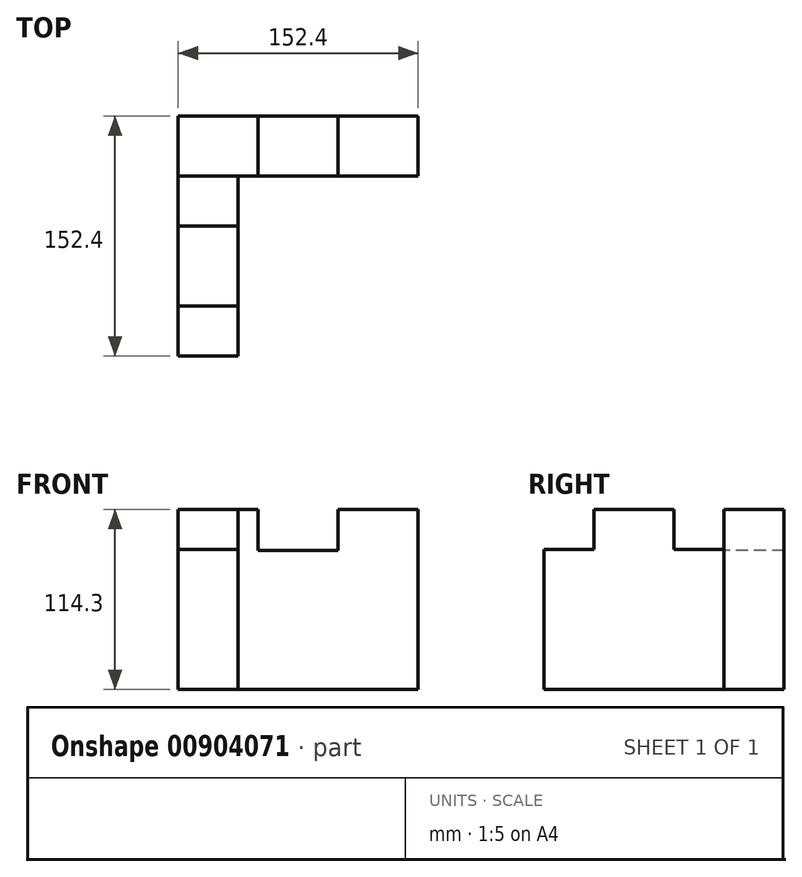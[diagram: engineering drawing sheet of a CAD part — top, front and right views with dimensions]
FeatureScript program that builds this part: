
annotation { "Feature Type Name" : "Feature", "Feature Type Description" : "" }
export const myFeature = defineFeature(function(context is Context, id is Id, definition is map)
    precondition{}
    {
        {
            var Q0;
            Q0=qCreatedBy(makeId("Front.planeOp"),FACE);
            var sketch = newSketch(context, id + "F0", { "sketchPlane" : qUnion([Q0])});
            skLineSegment(sketch, "E0.bottom", {"start": v(-76.2, 57.15) * mm, "end": v(76.2, 57.15) * mm});
            skLineSegment(sketch, "E0.top", {"start": v(-76.2, -57.15) * mm, "end": v(76.2, -57.15) * mm});
            skLineSegment(sketch, "E0.left", {"start": v(-76.2, 57.15) * mm, "end": v(-76.2, -57.15) * mm});
            skLineSegment(sketch, "E0.right", {"start": v(76.2, 57.15) * mm, "end": v(76.2, -57.15) * mm});
            skPoint(sketch, "E0.middle", {"position": v(0, 0) * mm});
            skSolve(sketch);
        }
        {
            var Q0;
            Q0=makeQuery(id+"F0.imprint","IMPRINT",FACE,{"disambiguationData":[TD([[makeQuery(id+"F0.imprint","IMPRINT",EDGE,{"derivedFrom":sQuery(id+"F0.wireOp",EDGE,"E0.bottom")}),-1.0]])]});
            extrude(context, id + "F1", {"entities" : qUnion([Q0]), "depth" : 152.4 * mm, "offsetDistance" : 25.4 * mm});
        }
        {
            var Q0;
            Q0=makeQuery(id+"F1.opExtrude","CAP_FACE",FACE,{"disambiguationData":[OSD([sQuery(id+"F0.wireOp",EDGE,"E0.bottom"),sQuery(id+"F0.wireOp",EDGE,"E0.top"),sQuery(id+"F0.wireOp",EDGE,"E0.left"),sQuery(id+"F0.wireOp",EDGE,"E0.right")])],"isStart":false});
            var sketch = newSketch(context, id + "F2", { "sketchPlane" : qUnion([Q0])});
            skLineSegment(sketch, "E1", {"start": v(-76.2, 57.15) * mm, "end": v(-38.1, 57.15) * mm});
            skLineSegment(sketch, "E2", {"start": v(-38.1, 57.15) * mm, "end": v(-38.1, -57.15) * mm});
            skSolve(sketch);
        }
        {
            var Q0;
            Q0 = qSketchRegion(id + "F2", true);
            var Q1;
            {var subQ0=sQuery(id+"F2.wireOp",EDGE,"E2");Q1=makeQuery(id+"F2.imprint","IMPRINT",FACE,{"disambiguationData":[TD([[makeQuery(id+"F2.imprint","IMPRINT",EDGE,{"derivedFrom":subQ0}),1.0]])]});}
            extrude(context, id + "F3", {"entities" : qUnion([Q0, Q1]), "operationType" : NewBodyOperationType.REMOVE, "oppositeDirection" : true, "depth" : 114.3 * mm, "offsetDistance" : 25.4 * mm});
        }
        {
            var Q0;
            Q0=makeQuery(id+"F1.opExtrude","CAP_FACE",FACE,{"disambiguationData":[OSD([sQuery(id+"F0.wireOp",EDGE,"E0.bottom"),sQuery(id+"F0.wireOp",EDGE,"E0.top"),sQuery(id+"F0.wireOp",EDGE,"E0.left"),sQuery(id+"F0.wireOp",EDGE,"E0.right")])],"isStart":false});
            var sketch = newSketch(context, id + "F4", { "sketchPlane" : qUnion([Q0])});
            skLineSegment(sketch, "E3.bottom", {"start": v(-76.2, 57.15) * mm, "end": v(-38.1, 57.15) * mm});
            skLineSegment(sketch, "E3.top", {"start": v(-76.2, 31.75) * mm, "end": v(-38.1, 31.75) * mm});
            skLineSegment(sketch, "E3.left", {"start": v(-76.2, 57.15) * mm, "end": v(-76.2, 31.75) * mm});
            skLineSegment(sketch, "E3.right", {"start": v(-38.1, 57.15) * mm, "end": v(-38.1, 31.75) * mm});
            skSolve(sketch);
        }
        {
            var Q0;
            Q0=makeQuery(id+"F4.imprint","IMPRINT",FACE,{"disambiguationData":[TD([[makeQuery(id+"F4.imprint","IMPRINT",EDGE,{"derivedFrom":sQuery(id+"F4.wireOp",EDGE,"E3.bottom")}),-1.0]])]});
            extrude(context, id + "F5", {"entities" : qUnion([Q0]), "operationType" : NewBodyOperationType.REMOVE, "oppositeDirection" : true, "depth" : 31.75 * mm, "offsetDistance" : 25.4 * mm});
        }
        {
            var Q0;
            Q0=makeQuery(id+"F3.boolean.opBoolean","COPY",FACE,{"derivedFrom":makeQuery(id+"F3.opExtrude","SWEPT_FACE",FACE,{"disambiguationData":[OSD([sQuery(id+"F2.wireOp",EDGE,"E2")])]})});
            var sketch = newSketch(context, id + "F6", { "sketchPlane" : qUnion([Q0])});
            skLineSegment(sketch, "E4.bottom", {"start": v(-38.1, 57.15) * mm, "end": v(-69.85, 57.15) * mm});
            skLineSegment(sketch, "E4.top", {"start": v(-38.1, 31.75) * mm, "end": v(-69.85, 31.75) * mm});
            skLineSegment(sketch, "E4.left", {"start": v(-38.1, 57.15) * mm, "end": v(-38.1, 31.75) * mm});
            skLineSegment(sketch, "E4.right", {"start": v(-69.85, 57.15) * mm, "end": v(-69.85, 31.75) * mm});
            skSolve(sketch);
        }
        {
            var Q0;
            Q0=makeQuery(id+"F6.imprint","IMPRINT",FACE,{"disambiguationData":[TD([[makeQuery(id+"F6.imprint","IMPRINT",EDGE,{"derivedFrom":sQuery(id+"F6.wireOp",EDGE,"E4.bottom")}),1.0]])]});
            extrude(context, id + "F7", {"entities" : qUnion([Q0]), "operationType" : NewBodyOperationType.REMOVE, "endBound" : BoundingType.THROUGH_ALL, "oppositeDirection" : true, "depth" : 25.4 * mm, "offsetDistance" : 25.4 * mm});
        }
        {
            var Q0;
            Q0=makeQuery(id+"F7.boolean.opBoolean","MERGE",FACE,{"derivedFrom":[makeQuery(id+"F3.boolean.opBoolean","COPY",FACE,{"derivedFrom":makeQuery(id+"F3.opExtrude","CAP_FACE",FACE,{"disambiguationData":[OSD([sQuery(id+"F0.wireOp",EDGE,"E0.bottom"),sQuery(id+"F0.wireOp",EDGE,"E0.top"),sQuery(id+"F0.wireOp",EDGE,"E0.right"),sQuery(id+"F2.wireOp",EDGE,"E2")])],"isStart":false})})],"fromTools":[makeQuery(id+"F7.opExtrude","SWEPT_FACE",FACE,{"disambiguationData":[OSD([sQuery(id+"F6.wireOp",EDGE,"E4.left")])]})]});
            var sketch = newSketch(context, id + "F8", { "sketchPlane" : qUnion([Q0])});
            skLineSegment(sketch, "E5.bottom", {"start": v(-25.4, 57.15) * mm, "end": v(25.4, 57.15) * mm});
            skLineSegment(sketch, "E5.top", {"start": v(-25.4, 31.08) * mm, "end": v(25.4, 31.08) * mm});
            skLineSegment(sketch, "E5.left", {"start": v(-25.4, 57.15) * mm, "end": v(-25.4, 31.08) * mm});
            skLineSegment(sketch, "E5.right", {"start": v(25.4, 57.15) * mm, "end": v(25.4, 31.08) * mm});
            skSolve(sketch);
        }
        {
            var Q0;
            Q0=makeQuery(id+"F8.imprint","IMPRINT",FACE,{"disambiguationData":[TD([[makeQuery(id+"F8.imprint","IMPRINT",EDGE,{"derivedFrom":sQuery(id+"F8.wireOp",EDGE,"E5.bottom")}),-1.0]])]});
            extrude(context, id + "F9", {"entities" : qUnion([Q0]), "operationType" : NewBodyOperationType.REMOVE, "endBound" : BoundingType.THROUGH_ALL, "oppositeDirection" : true, "depth" : 25.4 * mm, "offsetDistance" : 25.4 * mm});
        }
    });
